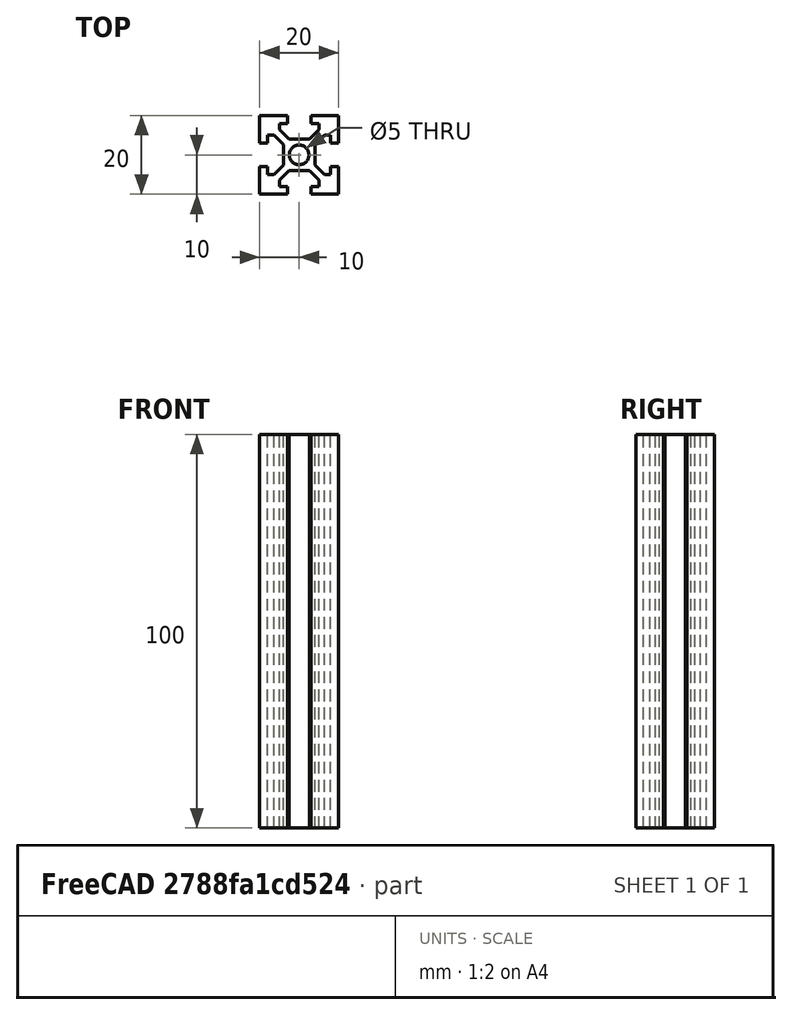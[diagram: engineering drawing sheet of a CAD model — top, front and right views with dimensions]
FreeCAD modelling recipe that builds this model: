
FCSTD DOCUMENT  (FreeCAD 0.19R24276 (Git))
Label: AL_profil_20_L570
License: All rights reserved
LicenseURL: http://en.wikipedia.org/wiki/All_rights_reserved
objects: Sketcher::SketchObject×1, PartDesign::Pad×1, PartDesign::Body×1
note: 4 computed .brp shape members not serialized (recipe doc carries the construction recipe); baked Part::Feature solids carry a one-line shape summary decoded from their .brp

FEATURE [Sketcher::SketchObject] Sketch
  FullyConstrained = false
  MapMode = 5
  Support = -> [XY_Plane]
  sketch-geometry (106):
    g0: LineSegment StartX=10 StartY=10 StartZ=0 EndX=-10 EndY=10 EndZ=0
    g1: LineSegment StartX=-10 StartY=10 StartZ=0 EndX=-10 EndY=-10 EndZ=0
    g2: LineSegment StartX=-10 StartY=-10 StartZ=0 EndX=10 EndY=-10 EndZ=0
    g3: LineSegment StartX=10 StartY=-10 StartZ=0 EndX=10 EndY=10 EndZ=0
    g4: Circle CenterX=0 CenterY=0 CenterZ=0 NormalX=0 NormalY=0 NormalZ=1 AngleXU=0 Radius=14.1421
    g5: LineSegment StartX=4 StartY=4 StartZ=0 EndX=-4 EndY=4 EndZ=0
    g6: LineSegment StartX=-4 StartY=4 StartZ=0 EndX=-4 EndY=-4 EndZ=0
    g7: LineSegment StartX=-4 StartY=-4 StartZ=0 EndX=4 EndY=-4 EndZ=0
    g8: LineSegment StartX=4 StartY=-4 StartZ=0 EndX=4 EndY=4 EndZ=0
    g9: Circle CenterX=0 CenterY=0 CenterZ=0 NormalX=0 NormalY=0 NormalZ=1 AngleXU=0 Radius=5.65685
    g10: Circle CenterX=0 CenterY=0 CenterZ=0 NormalX=0 NormalY=0 NormalZ=1 AngleXU=0 Radius=2.5
    g11: LineSegment StartX=-10 StartY=-10 StartZ=0 EndX=-5 EndY=-10 EndZ=0
    g12: LineSegment StartX=-5 StartY=-10 StartZ=0 EndX=-5 EndY=-5 EndZ=0
    g13: LineSegment StartX=-5 StartY=-5 StartZ=0 EndX=-10 EndY=-5 EndZ=0
    g14: LineSegment StartX=-10 StartY=-5 StartZ=0 EndX=-10 EndY=-10 EndZ=0
    g15: LineSegment StartX=10 StartY=-10 StartZ=0 EndX=5 EndY=-10 EndZ=0
    g16: LineSegment StartX=5 StartY=-8 StartZ=0 EndX=5 EndY=-5 EndZ=0
    g17: LineSegment StartX=5 StartY=-5 StartZ=0 EndX=10 EndY=-5 EndZ=0
    g18: LineSegment StartX=10 StartY=-5 StartZ=0 EndX=10 EndY=-10 EndZ=0
    g19: LineSegment StartX=10 StartY=10 StartZ=0 EndX=5 EndY=10 EndZ=0
    g20: LineSegment StartX=5 StartY=10 StartZ=0 EndX=5 EndY=5 EndZ=0
    g21: LineSegment StartX=5 StartY=5 StartZ=0 EndX=10 EndY=5 EndZ=0
    g22: LineSegment StartX=10 StartY=5 StartZ=0 EndX=10 EndY=10 EndZ=0
    g23: LineSegment StartX=-10 StartY=10 StartZ=0 EndX=-5 EndY=10 EndZ=0
    g24: LineSegment StartX=-5 StartY=10 StartZ=0 EndX=-5 EndY=5 EndZ=0
    g25: LineSegment StartX=-5 StartY=5 StartZ=0 EndX=-10 EndY=5 EndZ=0
    g26: LineSegment StartX=-10 StartY=5 StartZ=0 EndX=-10 EndY=10 EndZ=0
    g27: LineSegment StartX=-6.41421 StartY=-5 StartZ=0 EndX=-4 EndY=-2.58579 EndZ=0
    g28: LineSegment StartX=-5 StartY=-6.41421 StartZ=0 EndX=-2.58579 EndY=-4 EndZ=0
    g29: LineSegment StartX=-5 StartY=-5 StartZ=0 EndX=-4 EndY=-4 EndZ=0
    g30: LineSegment StartX=-4 StartY=-4 StartZ=0 EndX=-5.70711 EndY=-5.70711 EndZ=0
    g31: LineSegment StartX=-6.41421 StartY=5 StartZ=0 EndX=-4 EndY=2.58579 EndZ=0
    g32: LineSegment StartX=-5 StartY=6.41421 StartZ=0 EndX=-2.58579 EndY=4 EndZ=0
    g33: LineSegment StartX=-5 StartY=5 StartZ=0 EndX=-4 EndY=4 EndZ=0
    g34: LineSegment StartX=-4 StartY=4 StartZ=0 EndX=-5.70711 EndY=5.70711 EndZ=0
    g35: LineSegment StartX=6.41421 StartY=-5 StartZ=0 EndX=4 EndY=-2.58579 EndZ=0
    g36: LineSegment StartX=5 StartY=-6.41421 StartZ=0 EndX=2.58579 EndY=-4 EndZ=0
    g37: LineSegment StartX=5 StartY=-5 StartZ=0 EndX=4 EndY=-4 EndZ=0
    g38: LineSegment StartX=4 StartY=-4 StartZ=0 EndX=5.70711 EndY=-5.70711 EndZ=0
    g39: LineSegment StartX=6.41421 StartY=5 StartZ=0 EndX=4 EndY=2.58579 EndZ=0
    g40: LineSegment StartX=5 StartY=6.41421 StartZ=0 EndX=2.58579 EndY=4 EndZ=0
    g41: LineSegment StartX=5 StartY=5 StartZ=0 EndX=4 EndY=4 EndZ=0
    g42: LineSegment StartX=4 StartY=4 StartZ=0 EndX=5.70711 EndY=5.70711 EndZ=0
    g43: LineSegment StartX=10 StartY=-10 StartZ=0 EndX=3 EndY=-10 EndZ=0
    g44: LineSegment StartX=3 StartY=-10 StartZ=0 EndX=3 EndY=-8 EndZ=0
    g45: LineSegment StartX=3 StartY=-8 StartZ=0 EndX=5 EndY=-8 EndZ=0
    g46: LineSegment StartX=10 StartY=-8 StartZ=0 EndX=10 EndY=-10 EndZ=0
    g47: LineSegment StartX=10 StartY=-3 StartZ=0 EndX=8 EndY=-3 EndZ=0
    g48: LineSegment StartX=8 StartY=-3 StartZ=0 EndX=8 EndY=-5 EndZ=0
    g49: LineSegment StartX=3 StartY=-10 StartZ=0 EndX=3 EndY=-8 EndZ=0
    g50: LineSegment StartX=3 StartY=-8 StartZ=0 EndX=5 EndY=-8 EndZ=0
    g51: LineSegment StartX=5 StartY=-8 StartZ=0 EndX=5 EndY=-6.41421 EndZ=0
    g52: LineSegment StartX=5 StartY=-6.41421 StartZ=0 EndX=2.58579 EndY=-4 EndZ=0
    g53: LineSegment StartX=4 StartY=-2.58579 StartZ=0 EndX=6.41421 EndY=-5 EndZ=0
    g54: LineSegment StartX=6.41421 StartY=-5 StartZ=0 EndX=8 EndY=-5 EndZ=0
    g55: LineSegment StartX=8 StartY=-5 StartZ=0 EndX=8 EndY=-3 EndZ=0
    g56: LineSegment StartX=8 StartY=-3 StartZ=0 EndX=10 EndY=-3 EndZ=0
    g57: LineSegment StartX=-2.58579 StartY=-4 StartZ=0 EndX=2.58579 EndY=-4 EndZ=0
    g58: LineSegment StartX=3 StartY=10 StartZ=0 EndX=3 EndY=8 EndZ=0
    g59: LineSegment StartX=3 StartY=8 StartZ=0 EndX=5 EndY=8 EndZ=0
    g60: LineSegment StartX=3 StartY=10 StartZ=0 EndX=3 EndY=8 EndZ=0
    g61: LineSegment StartX=3 StartY=8 StartZ=0 EndX=5 EndY=8 EndZ=0
    g62: LineSegment StartX=10 StartY=3 StartZ=0 EndX=8 EndY=3 EndZ=0
    g63: LineSegment StartX=8 StartY=3 StartZ=0 EndX=8 EndY=5 EndZ=0
    g64: LineSegment StartX=8 StartY=5 StartZ=0 EndX=8 EndY=3 EndZ=0
    g65: LineSegment StartX=8 StartY=3 StartZ=0 EndX=10 EndY=3 EndZ=0
    g66: LineSegment StartX=2.58579 StartY=4 StartZ=0 EndX=5 EndY=6.41421 EndZ=0
    g67: LineSegment StartX=5 StartY=6.41421 StartZ=0 EndX=5 EndY=8 EndZ=0
    g68: LineSegment StartX=-2.58579 StartY=4 StartZ=0 EndX=2.58579 EndY=4 EndZ=0
    g69: LineSegment StartX=4 StartY=2.58579 StartZ=0 EndX=6.41421 EndY=5 EndZ=0
    g70: LineSegment StartX=6.41421 StartY=5 StartZ=0 EndX=8 EndY=5 EndZ=0
    g71: LineSegment StartX=4 StartY=-2.58579 StartZ=0 EndX=4 EndY=2.58579 EndZ=0
    g72: LineSegment StartX=10 StartY=3 StartZ=0 EndX=10 EndY=10 EndZ=0
    g73: LineSegment StartX=10 StartY=-10 StartZ=0 EndX=10 EndY=-3 EndZ=0
    g74: LineSegment StartX=-3 StartY=-10 StartZ=0 EndX=-3 EndY=-8 EndZ=0
    g75: LineSegment StartX=-3 StartY=-8 StartZ=0 EndX=-5 EndY=-8 EndZ=0
    g76: LineSegment StartX=-3 StartY=-10 StartZ=0 EndX=-3 EndY=-8 EndZ=0
    g77: LineSegment StartX=-3 StartY=-8 StartZ=0 EndX=-5 EndY=-8 EndZ=0
    g78: LineSegment StartX=-5 StartY=-8 StartZ=0 EndX=-5 EndY=-6.41421 EndZ=0
    g79: LineSegment StartX=-10 StartY=-3 StartZ=0 EndX=-8 EndY=-3 EndZ=0
    g80: LineSegment StartX=-8 StartY=-3 StartZ=0 EndX=-8 EndY=-5 EndZ=0
    g81: LineSegment StartX=-6.41421 StartY=-5 StartZ=0 EndX=-8 EndY=-5 EndZ=0
    g82: LineSegment StartX=-8 StartY=-5 StartZ=0 EndX=-8 EndY=-3 EndZ=0
    g83: LineSegment StartX=-8 StartY=-3 StartZ=0 EndX=-10 EndY=-3 EndZ=0
    g84: LineSegment StartX=-10 StartY=10 StartZ=0 EndX=10 EndY=10 EndZ=0
    g85: LineSegment StartX=-6.41421 StartY=-5 StartZ=0 EndX=-4 EndY=-2.58579 EndZ=0
    g86: LineSegment StartX=-4 StartY=2.58579 StartZ=0 EndX=-4 EndY=-2.58579 EndZ=0
    g87: LineSegment StartX=-5 StartY=-6.41421 StartZ=0 EndX=-2.58579 EndY=-4 EndZ=0
    g88: LineSegment StartX=3 StartY=-10 StartZ=0 EndX=10 EndY=-10 EndZ=0
    g89: LineSegment StartX=-3 StartY=-10 StartZ=0 EndX=-10 EndY=-10 EndZ=0
    g90: LineSegment StartX=-10 StartY=3 StartZ=0 EndX=-8 EndY=3 EndZ=0
    g91: LineSegment StartX=-8 StartY=3 StartZ=0 EndX=-8 EndY=5 EndZ=0
    g92: LineSegment StartX=-8 StartY=5 StartZ=0 EndX=-8 EndY=3 EndZ=0
    g93: LineSegment StartX=-8 StartY=3 StartZ=0 EndX=-10 EndY=3 EndZ=0
    g94: LineSegment StartX=-3 StartY=10 StartZ=0 EndX=-3 EndY=8 EndZ=0
    g95: LineSegment StartX=-3 StartY=8 StartZ=0 EndX=-5 EndY=8 EndZ=0
    g96: LineSegment StartX=-3 StartY=10 StartZ=0 EndX=-3 EndY=8 EndZ=0
    g97: LineSegment StartX=-3 StartY=8 StartZ=0 EndX=-5 EndY=8 EndZ=0
    g98: LineSegment StartX=-5 StartY=8 StartZ=0 EndX=-5 EndY=6.41421 EndZ=0
    g99: LineSegment StartX=-6.41421 StartY=5 StartZ=0 EndX=-8 EndY=5 EndZ=0
    g100: LineSegment StartX=-5 StartY=6.41421 StartZ=0 EndX=-2.58579 EndY=4 EndZ=0
    g101: LineSegment StartX=-6.41421 StartY=5 StartZ=0 EndX=-4 EndY=2.58579 EndZ=0
    g102: LineSegment StartX=-10 StartY=-3 StartZ=0 EndX=-10 EndY=-10 EndZ=0
    g103: LineSegment StartX=-10 StartY=3 StartZ=0 EndX=-10 EndY=10 EndZ=0
    g104: LineSegment StartX=-10 StartY=10 StartZ=0 EndX=-3 EndY=10 EndZ=0
    g105: LineSegment StartX=3 StartY=10 StartZ=0 EndX=10 EndY=10 EndZ=0
  constraints (271):
    c: Coincident(g0,g1)
    c: Coincident(g1,g2)
    c: Coincident(g2,g3)
    c: Coincident(g3,g0)
    c: Equal(g0,g1)
    c: Equal(g0,g2)
    c: Equal(g0,g3)
    c: PointOnObject(g0,g4)
    c: PointOnObject(g1,g4)
    c: PointOnObject(g2,g4)
    c: PointOnObject(g3,g4)
    c: Coincident(g4,g-1)
    c: Horizontal(g0)
    c: Coincident(g5,g6)
    c: Coincident(g6,g7)
    c: Coincident(g7,g8)
    c: Coincident(g8,g5)
    c: Equal(g5,g6)
    c: Equal(g5,g7)
    c: Equal(g5,g8)
    c: PointOnObject(g5,g9)
    c: PointOnObject(g6,g9)
    c: PointOnObject(g7,g9)
    c: PointOnObject(g8,g9)
    c: Coincident(g9,g-1)
    c: Horizontal(g5)
    c: DistanceX(g5,g5) = 8
    c: Diameter(g10) = 5
    c: DistanceX(g2,g2) = 20
    c: Coincident(g10,g-1)
    c: Coincident(g11,g12)
    c: Coincident(g12,g13)
    c: Coincident(g13,g14)
    c: Coincident(g14,g11)
    c: Horizontal(g11)
    c: Horizontal(g13)
    c: Vertical(g12)
    c: Vertical(g14)
    c: Coincident(g11,g1)
    c: Coincident(g16,g17)
    c: Coincident(g17,g18)
    c: Coincident(g18,g15)
    c: Horizontal(g15)
    c: Horizontal(g17)
    c: Vertical(g16)
    c: Vertical(g18)
    c: Coincident(g15,g2)
    c: Coincident(g19,g20)
    c: Coincident(g20,g21)
    c: Coincident(g21,g22)
    c: Coincident(g22,g19)
    c: Horizontal(g19)
    c: Horizontal(g21)
    c: Vertical(g20)
    c: Vertical(g22)
    c: Coincident(g19,g0)
    c: Coincident(g23,g24)
    c: Coincident(g24,g25)
    c: Coincident(g25,g26)
    c: Coincident(g26,g23)
    c: Horizontal(g23)
    c: Horizontal(g25)
    c: Vertical(g24)
    c: Vertical(g26)
    c: Coincident(g23,g0)
    c: DistanceX(g1,g11) = 5
    c: Equal(g12,g13)
    c: Equal(g13,g17)
    c: Equal(g25,g13)
    c: Equal(g13,g21)
    c: Equal(g24,g20)
    c: Equal(g20,g12)
    c: Parallel(g27,g28)
    c: Coincident(g29,g12)
    c: Coincident(g29,g6)
    c: Parallel(g27,g29)
    c: Coincident(g30,g6)
    c: Parallel(g29,g30)
    c: PointOnObject(g28,g12)
    c: PointOnObject(g27,g13)
    c: Distance(g28,g27) = 2
    c: PointOnObject(g27,g6)
    c: PointOnObject(g28,g7)
    c: Symmetric(g27,g28,g30)
    c: Parallel(g31,g32)
    c: Parallel(g31,g33)
    c: Parallel(g33,g34)
    c: Coincident(g33,g34)
    c: Coincident(g33,g5)
    c: Coincident(g33,g24)
    c: PointOnObject(g31,g25)
    c: PointOnObject(g32,g24)
    c: PointOnObject(g32,g5)
    c: PointOnObject(g31,g6)
    c: Symmetric(g31,g32,g34)
    c: Distance(g31,g32) = 2
    c: Parallel(g35,g36)
    c: Parallel(g35,g37)
    c: Parallel(g37,g38)
    c: Parallel(g39,g40)
    c: Parallel(g39,g41)
    c: Parallel(g41,g42)
    c: Coincident(g41,g42)
    c: Coincident(g41,g5)
    c: PointOnObject(g40,g5)
    c: PointOnObject(g39,g8)
    c: PointOnObject(g39,g21)
    c: PointOnObject(g40,g20)
    c: Coincident(g20,g41)
    c: Distance(g40,g39) = 2
    c: Symmetric(g40,g39,g42)
    c: PointOnObject(g35,g8)
    c: PointOnObject(g35,g17)
    c: PointOnObject(g36,g16)
    c: PointOnObject(g36,g7)
    c: Coincident(g38,g37)
    c: Coincident(g38,g7)
    c: Coincident(g37,g16)
    c: Symmetric(g36,g35,g38)
    c: Distance(g36,g35) = 2
    c: Coincident(g43,g44)
    c: Coincident(g44,g45)
    c: Coincident(g46,g43)
    c: Horizontal(g43)
    c: Horizontal(g45)
    c: Vertical(g44)
    c: Vertical(g46)
    c: Coincident(g43,g2)
    c: DistanceX(g43,g2) = 7
    c: DistanceY(g2,g46) = 2
    c: Coincident(g45,g16)
    c: Coincident(g47,g48)
    c: Equal(g44,g47)
    c: Vertical(g48)
    c: Horizontal(g47)
    c: Vertical(g47,g2)
    c: Horizontal(g17,g13)
    c: PointOnObject(g48,g17)
    c: DistanceY(g2,g47) = 7
    c: DistanceX(g47,g47) = 2
    c: Coincident(g49,g43)
    c: Coincident(g50,g44)
    c: Coincident(g51,g50)
    c: Coincident(g52,g51)
    c: Coincident(g53,g35)
    c: Coincident(g54,g53)
    c: Coincident(g55,g48)
    c: Coincident(g56,g55)
    c: Coincident(g49,g50)
    c: Coincident(g50,g16)
    c: Coincident(g51,g36)
    c: Coincident(g52,g36)
    c: Coincident(g53,g35)
    c: Coincident(g54,g55)
    c: Coincident(g55,g47)
    c: Coincident(g56,g47)
    c: Coincident(g57,g28)
    c: Coincident(g57,g52)
    c: Coincident(g58,g59)
    c: Horizontal(g59)
    c: Vertical(g58)
    c: Coincident(g62,g63)
    c: Equal(g58,g62)
    c: Vertical(g63)
    c: Horizontal(g62)
    c: Coincident(g61,g58)
    c: Coincident(g64,g63)
    c: Coincident(g65,g64)
    c: Coincident(g60,g61)
    c: Coincident(g64,g62)
    c: Coincident(g65,g62)
    c: Equal(g56,g65)
    c: Vertical(g65,g56)
    c: Equal(g55,g64)
    c: Horizontal(g64,g21)
    c: Equal(g61,g64)
    c: Horizontal(g60,g19)
    c: Coincident(g60,g58)
    c: Coincident(g61,g59)
    c: Vertical(g61,g19)
    c: Coincident(g66,g40)
    c: Coincident(g67,g66)
    c: Coincident(g67,g61)
    c: Coincident(g66,g40)
    c: Coincident(g68,g32)
    c: Coincident(g68,g66)
    c: Coincident(g69,g39)
    c: Coincident(g70,g69)
    c: Coincident(g69,g39)
    c: Coincident(g70,g64)
    c: Coincident(g71,g53)
    c: Coincident(g71,g69)
    c: Coincident(g72,g65)
    c: Coincident(g72,g0)
    c: Coincident(g73,g2)
    c: Coincident(g73,g56)
    c: Horizontal(g84)
    c: Coincident(g74,g75)
    c: Horizontal(g75)
    c: Vertical(g74)
    c: Coincident(g79,g80)
    c: Equal(g74,g79)
    c: Vertical(g80)
    c: Horizontal(g79)
    c: Coincident(g77,g74)
    c: Coincident(g78,g77)
    c: Coincident(g82,g80)
    c: Coincident(g83,g82)
    c: Coincident(g76,g77)
    c: Coincident(g81,g82)
    c: Coincident(g82,g79)
    c: Coincident(g83,g79)
    c: Horizontal(g76,g49)
    c: Horizontal(g76,g49)
    c: Vertical(g78)
    c: Coincident(g77,g75)
    c: Coincident(g78,g28)
    c: Equal(g77,g50)
    c: Vertical(g83,g1)
    c: Coincident(g74,g76)
    c: Equal(g82,g77)
    c: Horizontal(g81)
    c: Coincident(g81,g27)
    c: Coincident(g85,g81)
    c: Coincident(g85,g27)
    c: Coincident(g86,g31)
    c: Coincident(g86,g85)
    c: Coincident(g87,g78)
    c: Coincident(g87,g57)
    c: Coincident(g88,g49)
    c: Coincident(g89,g76)
    c: Coincident(g1,g89)
    c: Coincident(g88,g73)
    c: Coincident(g94,g95)
    c: Horizontal(g95)
    c: Vertical(g94)
    c: Coincident(g90,g91)
    c: Equal(g94,g90)
    c: Vertical(g91)
    c: Horizontal(g90)
    c: Coincident(g97,g94)
    c: Coincident(g98,g97)
    c: Coincident(g92,g91)
    c: Coincident(g93,g92)
    c: Coincident(g96,g97)
    c: Coincident(g99,g92)
    c: Coincident(g92,g90)
    c: Coincident(g93,g90)
    c: Vertical(g98)
    c: Coincident(g97,g95)
    c: Coincident(g94,g96)
    c: Equal(g92,g97)
    c: Horizontal(g99)
    c: Horizontal(g96,g23)
    c: Equal(g97,g61)
    c: Horizontal(g60,g96)
    c: Coincident(g98,g32)
    c: Coincident(g100,g98)
    c: Coincident(g68,g100)
    c: Coincident(g99,g31)
    c: Vertical(g92,g82)
    c: Coincident(g101,g99)
    c: Coincident(g101,g86)
    c: Coincident(g102,g83)
    c: Coincident(g103,g93)
    c: Coincident(g104,g0)
    c: Coincident(g105,g60)
    c: Coincident(g103,g104)
    c: Coincident(g102,g89)
    c: Coincident(g104,g96)
    c: Coincident(g105,g72)
FEATURE [PartDesign::Pad] Pad
  Direction = (1,1,1)
  Length = 100
  Length2 = 100
  Profile = -> Sketch
  Type = 0
FEATURE [PartDesign::Body] Body
  Group = -> [Sketch,Pad]
  Origin = -> Origin
  Tip = -> Pad
